# Revit family: HVAC_Mechanical-Ventilation_Ice-Air_WSHP_Vertical-Stack
name_source: partatom
category: Mechanical Equipment
revit_build: Autodesk Revit 2015 (Build: 20140606_1530(x64)
units: mm (PartAtom-declared; Revit-internal decimal feet)

## types (7) — shared parameters
Actual Condensate Drain Flow = 0 GPM
Aluminum Material = Aluminum - Ice_Air - White
BIMobject category = Air Conditioning
BIMobject category code = hvac-air-con
BIMobject main category = HVAC
BIMobject main category code = hvac
Brand url = http://www.ice-air.com
Condensate Connection = 0.75 "
Date of publishing = 1/13/2014
Default Elevation = 48 "
Description = ICE AIRs Vertical Stack Water Source Heat Pump units provide an ideal solution for whisper quiet cooling and heating within a tight footprint.
Design country = United States
Edition number = 1
Floor Offset = 8 "
Frequency = 60 Hz
Front Panel Height = 60.5 "
Height = 88 "
IFC Classification = Heat Exchanger
Installation instructions = http://www.ice-air.com
Manufacturer = Ice Air
Manufacturer country = United States
Manufacturer name = Ice Air
Masterformat 2014 Code = 23 81 46
Masterformat 2014 Description = Water-Source Unitary Heat Pumps
Motor = 115V/60Hz
NBS Reference Code = 68-38
NBS Reference Description = Heat Pumps
OmniClass Code = 23-33 17 00
OmniClass Description = Heat Pumps
Phase = 1
Plastic Material = Plastic - Ice_Air - White
Product Guid = de243c38-3cdd-460f-b671-938ff739babc
Product SKU = vertical_stack_wshp
Product data url = https://bimobject.com
Product family = WSHP
Product group = Vertical Stack
Product url = http://www.ice-air.com
QR code = http://bimobject.com
Steel Material = Steel - Ice_Air - Galvanized
Technical description = http://www.ice-air.com
UNSPSC Code = 40101806
URL = http://www.ice-air.com
Uniclass 1.4 Code = L7524
Uniclass 1.4 Description = Heat pumps
Uniclass 2.0 Code = PR-68-38
Uniclass 2.0 Description = Heat Pumps
Uniclass 2015 Code = Pr_70_60_37
Uniclass 2015 Name = Heat pumps
Uniformat II Code = D3090
Uniformat II Description = Other HVAC Systems & Equipment
Voltage = 230 V
Voltage (Range) = 208 - 230 V
Weight Net (Kg) = 0
zero-valued in all types: Nominal height, Nominal width

## per-type parameters (varying)
| type | Air Flow | Coefficient of Performance | Depth | Discharge Width | Energy Efficiency Rating | Fan Power | Flow Rate | Inlet/Outlet Connection | Top Duct Height | Top Duct Width | Total Cooling Capacity | Total Heating Capacity | Weight | Width | z Type |
| 8VSHPW09 | 420 CFM | 4.4 | 17 " | 12 " | 14 | 35 W | 2 GPM | 0.5 " | 12 " | 12 " | 9500.0 Btu/h | 11900.0 Btu/h | 156.00 lbm | 16 " | 1 |
| 8VSHPW12 | 500 CFM | 4.2 | 17 " | 12 " | 13.7 | 35 W | 2 GPM | 0.5 " | 12 " | 12 " | 13200.0 Btu/h | 14700.0 Btu/h | 156.00 lbm | 16 " | 2 |
| 8VSHPW15 | 540 CFM | 4.5 | 17 " | 12 " | 14.4 | 35 W | 2 GPM | 0.5 " | 12 " | 12 " | 13700.0 Btu/h | 15400.0 Btu/h | 156.00 lbm | 16 " | 3 |
| 8VSHPW18 | 630 CFM | 4.4 | 20 " | 14 " | 14.4 | 150 W | 3 GPM | 0.75 " | 14 " | 14 " | 17600.0 Btu/h | 19100.0 Btu/h | 183.00 lbm | 18 " | 4 |
| 8VSHPW24 | 770 CFM | 4.1 | 20 " | 14 " | 13 | 150 W | 4 GPM | 0.75 " | 14 " | 14 " | 22700.0 Btu/h | 27200.0 Btu/h | 183.00 lbm | 18 " | 5 |
| 8VSHPW30 | 1000 CFM | 4.4 | 24 " | 18 " | 13.7 | 200 W | 5 GPM | 0.75 " | 14 " | 18 " | 27800.0 Btu/h | 31900.0 Btu/h | 260.00 lbm | 22 " | 6 |
| 8VSHPW36 | 1080 CFM | 3.8 | 24 " | 18 " | 12.9 | 200 W | 6 GPM | 0.75 " | 14 " | 18 " | 36500.0 Btu/h | 41800.0 Btu/h | 264.00 lbm | 22 " | 7 |

note: column(s) folded — value = type name in every type: Model

## geometry (parser evidence)
native form markers: Sweep x8
no freeform markers — native parametric forms only
